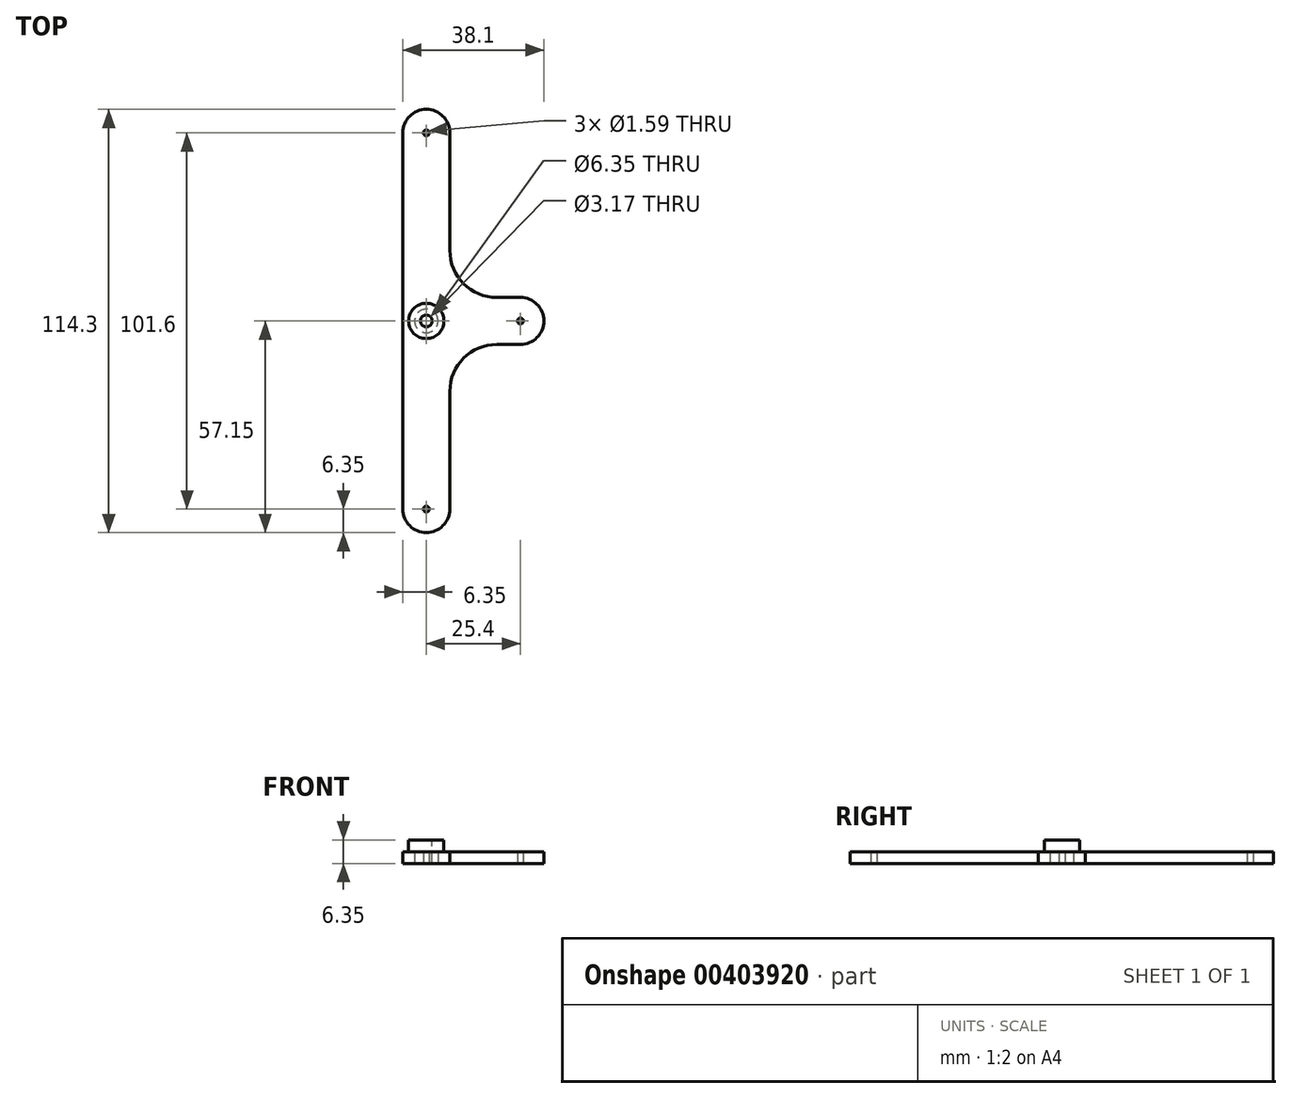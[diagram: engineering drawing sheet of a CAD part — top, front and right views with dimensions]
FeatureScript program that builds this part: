
annotation { "Feature Type Name" : "Feature", "Feature Type Description" : "" }
export const myFeature = defineFeature(function(context is Context, id is Id, definition is map)
    precondition{}
    {
        {
            var Q0;
            Q0=qCreatedBy(makeId("Top.planeOp"),FACE);
            var sketch = newSketch(context, id + "F0", { "sketchPlane" : qUnion([Q0])});
            skCircle(sketch, "E0", {"center": v(0, 0) * mm, "radius": 3.18 * mm});
            skSolve(sketch);
        }
        {
            var Q0;
            Q0 = qSketchRegion(id + "F0", true);
            extrude(context, id + "F1", {"entities" : qUnion([Q0]), "depth" : 3.17 * mm});
        }
        {
            var Q0;
            Q0=makeQuery(id+"F1.opExtrude","CAP_FACE",FACE,{"disambiguationData":[OSD([sQuery(id+"F0.wireOp",EDGE,"E0")])],"isStart":false});
            var sketch = newSketch(context, id + "F2", { "sketchPlane" : qUnion([Q0])});
            skCircle(sketch, "E1", {"center": v(0, 0) * mm, "radius": 4.76 * mm});
            skSolve(sketch);
        }
        {
            var Q0;
            Q0 = qSketchRegion(id + "F2", true);
            extrude(context, id + "F3", {"entities" : qUnion([Q0]), "operationType" : NewBodyOperationType.ADD, "depth" : 3.17 * mm});
        }
        {
            var Q0;
            Q0=makeQuery(id+"F3.opExtrude","CAP_FACE",FACE,{"disambiguationData":[OSD([sQuery(id+"F2.wireOp",EDGE,"E1")])],"isStart":false});
            var sketch = newSketch(context, id + "F4", { "sketchPlane" : qUnion([Q0])});
            skCircle(sketch, "E2", {"center": v(0, 0) * mm, "radius": 1.59 * mm});
            skSolve(sketch);
        }
        {
            var Q0;
            Q0 = qSketchRegion(id + "F4", true);
            extrude(context, id + "F5", {"entities" : qUnion([Q0]), "operationType" : NewBodyOperationType.REMOVE, "endBound" : BoundingType.THROUGH_ALL, "oppositeDirection" : true, "depth" : 25.4 * mm});
        }
        {
            var Q0;
            Q0=qCreatedBy(makeId("Top.planeOp"),FACE);
            var sketch = newSketch(context, id + "F6", { "sketchPlane" : qUnion([Q0])});
            skLineSegment(sketch, "E3.bottom", {"start": v(0, 57.15) * mm, "end": v(0, 57.15) * mm});
            skLineSegment(sketch, "E3.top", {"start": v(0, -57.15) * mm, "end": v(0, -57.15) * mm});
            skLineSegment(sketch, "E3.left", {"start": v(6.35, 50.8) * mm, "end": v(6.35, 19.05) * mm});
            skLineSegment(sketch, "E3.right", {"start": v(-6.35, 50.8) * mm, "end": v(-6.35, -50.8) * mm});
            skPoint(sketch, "E3.middle", {"position": v(0, 0) * mm});
            skLineSegment(sketch, "E4.bottom", {"start": v(19.05, 6.35) * mm, "end": v(25.4, 6.35) * mm});
            skLineSegment(sketch, "E4.top", {"start": v(19.05, -6.35) * mm, "end": v(25.4, -6.35) * mm});
            skLineSegment(sketch, "E4.right", {"start": v(31.75, 0) * mm, "end": v(31.75, 0) * mm});
            skPoint(sketch, "E4.middle", {"position": v(19.05, 0) * mm});
            skPoint(sketch, "E4.middle.positionSnap0", {"position": v(-6.35, 0) * mm});
            skPoint(sketch, "E4.centerSnap0", {"position": v(-6.35, 0) * mm});
            skPoint(sketch, "E5.visualSharp", {"position": v(-6.35, 57.15) * mm});
            skArc(sketch, "E5.filletArc", {"start": v(0, 57.15) * mm, "mid": v(-4.5, 55.3) * mm, "end": v(-6.35, 50.8) * mm});
            skPoint(sketch, "E6.visualSharp", {"position": v(6.35, 57.15) * mm});
            skArc(sketch, "E6.filletArc", {"start": v(6.35, 50.8) * mm, "mid": v(4.5, 55.3) * mm, "end": v(0, 57.15) * mm});
            skPoint(sketch, "E7.visualSharp", {"position": v(31.75, 6.35) * mm});
            skArc(sketch, "E7.filletArc", {"start": v(31.75, 0) * mm, "mid": v(29.9, 4.5) * mm, "end": v(25.4, 6.35) * mm});
            skPoint(sketch, "E8.visualSharp", {"position": v(31.75, -6.35) * mm});
            skArc(sketch, "E8.filletArc", {"start": v(25.4, -6.35) * mm, "mid": v(29.9, -4.5) * mm, "end": v(31.75, 0) * mm});
            skPoint(sketch, "E9.visualSharp", {"position": v(6.35, -57.15) * mm});
            skArc(sketch, "E9.filletArc", {"start": v(0, -57.15) * mm, "mid": v(4.5, -55.3) * mm, "end": v(6.35, -50.8) * mm});
            skPoint(sketch, "E10.visualSharp", {"position": v(-6.35, -57.15) * mm});
            skArc(sketch, "E10.filletArc", {"start": v(-6.35, -50.8) * mm, "mid": v(-4.5, -55.3) * mm, "end": v(0, -57.15) * mm});
            skLineSegment(sketch, "E11.trimOffspring", {"start": v(6.35, -19.05) * mm, "end": v(6.35, -50.8) * mm});
            skPoint(sketch, "E12.visualSharp", {"position": v(6.35, 6.35) * mm});
            skArc(sketch, "E12.filletArc", {"start": v(6.35, 19.05) * mm, "mid": v(10.07, 10.07) * mm, "end": v(19.05, 6.35) * mm});
            skPoint(sketch, "E13.visualSharp", {"position": v(6.35, -6.35) * mm});
            skArc(sketch, "E13.filletArc", {"start": v(19.05, -6.35) * mm, "mid": v(10.07, -10.07) * mm, "end": v(6.35, -19.05) * mm});
            skCircle(sketch, "E14.0", {"center": v(0, 0) * mm, "radius": 3.18 * mm});
            skCircle(sketch, "E15", {"center": v(0, 50.8) * mm, "radius": 0.8 * mm});
            skCircle(sketch, "E16", {"center": v(25.4, 0) * mm, "radius": 0.8 * mm});
            skCircle(sketch, "E17", {"center": v(0, -50.8) * mm, "radius": 0.8 * mm});
            skSolve(sketch);
        }
        {
            var Q0;
            Q0 = qSketchRegion(id + "F6", true);
            extrude(context, id + "F7", {"entities" : qUnion([Q0]), "depth" : 3.2 * mm});
        }
    });
